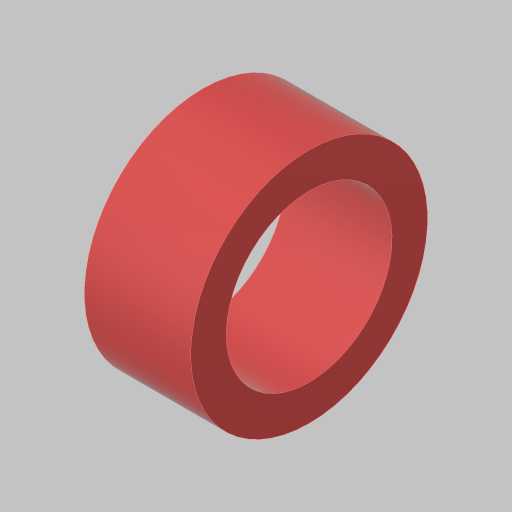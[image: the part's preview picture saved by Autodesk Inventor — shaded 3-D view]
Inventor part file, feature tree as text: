
AUTODESK INVENTOR PART (.ipt)
format: ipt  version: 2023.5 (Build 275446000, 446)  size: 110,592 bytes
history: native  units: in
note: dims shown in document units (in); Inventor stores cm internally (conversion verified against a paired STEP export)
features: extrude x1, sketch x1
ambient origin geometry x8: Origin, YZ Plane, XZ Plane, XY Plane, X Axis, Y Axis, Z Axis, Center Point
bodies: Solid1 (feature_tree)
feature tree (2):
  extrude  "Extrusion1"  Depth=0.375in
  sketch  "Sketch1"  dims[d0=0.585in d1=0.125in d2=0.375in d3=0.0in]
